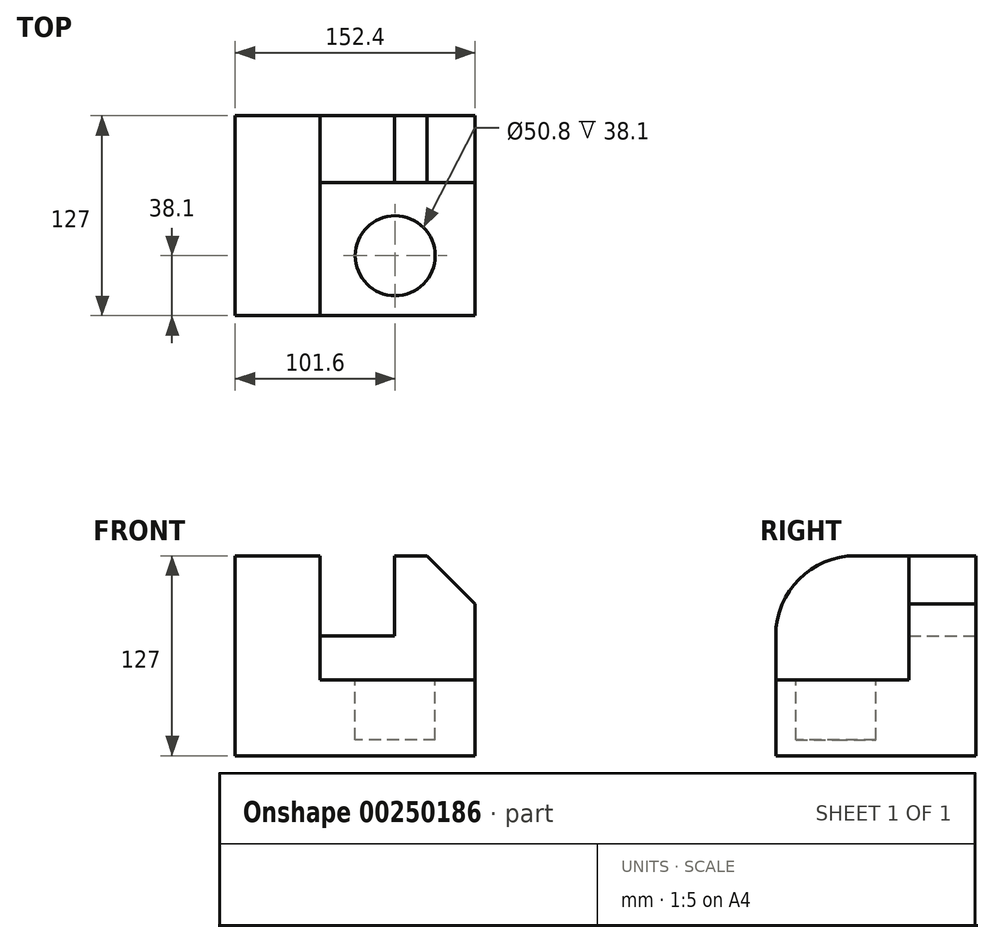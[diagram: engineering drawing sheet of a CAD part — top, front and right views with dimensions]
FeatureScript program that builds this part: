
annotation { "Feature Type Name" : "Feature", "Feature Type Description" : "" }
export const myFeature = defineFeature(function(context is Context, id is Id, definition is map)
    precondition{}
    {
        {
            var Q0;
            Q0=qCreatedBy(makeId("Top.planeOp"),FACE);
            var sketch = newSketch(context, id + "F0", { "sketchPlane" : qUnion([Q0])});
            skLineSegment(sketch, "E0.bottom", {"start": v(76.2, 63.5) * mm, "end": v(-76.2, 63.5) * mm});
            skLineSegment(sketch, "E0.top", {"start": v(76.2, -63.5) * mm, "end": v(-76.2, -63.5) * mm});
            skLineSegment(sketch, "E0.left", {"start": v(76.2, 63.5) * mm, "end": v(76.2, -63.5) * mm});
            skLineSegment(sketch, "E0.right", {"start": v(-76.2, 63.5) * mm, "end": v(-76.2, -63.5) * mm});
            skPoint(sketch, "E0.middle", {"position": v(0, 0) * mm});
            skSolve(sketch);
        }
        {
            var Q0;
            Q0=makeQuery(id+"F0.imprint","IMPRINT",FACE,{"disambiguationData":[TD([[makeQuery(id+"F0.imprint","IMPRINT",EDGE,{"derivedFrom":sQuery(id+"F0.wireOp",EDGE,"E0.bottom")}),1.0]])]});
            extrude(context, id + "F1", {"entities" : qUnion([Q0]), "depth" : 127 * mm});
        }
        {
            var Q0;
            Q0=makeQuery(id+"F1.opExtrude","CAP_FACE",FACE,{"disambiguationData":[OSD([sQuery(id+"F0.wireOp",EDGE,"E0.bottom"),sQuery(id+"F0.wireOp",EDGE,"E0.top"),sQuery(id+"F0.wireOp",EDGE,"E0.left"),sQuery(id+"F0.wireOp",EDGE,"E0.right")])],"isStart":false});
            var sketch = newSketch(context, id + "F2", { "sketchPlane" : qUnion([Q0])});
            skLineSegment(sketch, "E1.bottom", {"start": v(-76.2, -63.5) * mm, "end": v(-22.42, -63.5) * mm});
            skLineSegment(sketch, "E1.top", {"start": v(-76.2, -24.2) * mm, "end": v(-22.42, -24.2) * mm});
            skLineSegment(sketch, "E1.left", {"start": v(-76.2, -63.5) * mm, "end": v(-76.2, -24.2) * mm});
            skLineSegment(sketch, "E1.right", {"start": v(-22.42, -63.5) * mm, "end": v(-22.42, -24.2) * mm});
            skLineSegment(sketch, "E2.bottom", {"start": v(-22.42, -24.2) * mm, "end": v(-76.2, -24.2) * mm});
            skLineSegment(sketch, "E2.top", {"start": v(-22.42, 63.5) * mm, "end": v(-76.2, 63.5) * mm});
            skLineSegment(sketch, "E2.left", {"start": v(-22.42, -24.2) * mm, "end": v(-22.42, 63.5) * mm});
            skLineSegment(sketch, "E2.right", {"start": v(-76.2, -24.2) * mm, "end": v(-76.2, 63.5) * mm});
            skLineSegment(sketch, "E3.bottom", {"start": v(-22.42, 63.5) * mm, "end": v(25.1, 63.5) * mm});
            skLineSegment(sketch, "E3.top", {"start": v(-22.42, 21.07) * mm, "end": v(25.1, 21.07) * mm});
            skLineSegment(sketch, "E3.left", {"start": v(-22.42, 63.5) * mm, "end": v(-22.42, 21.07) * mm});
            skLineSegment(sketch, "E3.right", {"start": v(25.1, 63.5) * mm, "end": v(25.1, 21.07) * mm});
            skLineSegment(sketch, "E4.top", {"start": v(25.1, 21.07) * mm, "end": v(40.8, 21.07) * mm});
            skLineSegment(sketch, "E5.bottom", {"start": v(-22.42, 21.07) * mm, "end": v(76.2, 21.07) * mm});
            skLineSegment(sketch, "E5.top", {"start": v(-22.42, -63.5) * mm, "end": v(76.2, -63.5) * mm});
            skLineSegment(sketch, "E5.left", {"start": v(-22.42, 21.07) * mm, "end": v(-22.42, -63.5) * mm});
            skLineSegment(sketch, "E5.right", {"start": v(76.2, 21.07) * mm, "end": v(76.2, -63.5) * mm});
            skLineSegment(sketch, "E6", {"start": v(76.2, 63.5) * mm, "end": v(76.2, 21.07) * mm});
            skLineSegment(sketch, "E7", {"start": v(25.1, 63.5) * mm, "end": v(76.2, 63.5) * mm});
            skLineSegment(sketch, "E8", {"start": v(40.8, 21.07) * mm, "end": v(40.8, 63.5) * mm});
            skSolve(sketch);
        }
        {
            var Q0;
            {var subQ0=sQuery(id+"F2.wireOp",EDGE,"E5.top");Q0=makeQuery(id+"F2.imprint","IMPRINT",FACE,{"disambiguationData":[TD([[makeQuery(id+"F2.imprint","IMPRINT",EDGE,{"derivedFrom":subQ0}),-1.0]])]});}
            extrude(context, id + "F3", {"entities" : qUnion([Q0]), "operationType" : NewBodyOperationType.REMOVE, "oppositeDirection" : true, "depth" : 78.74 * mm});
        }
        {
            var Q0;
            Q0=makeQuery(id+"F2.imprint","IMPRINT",FACE,{"disambiguationData":[TD([[makeQuery(id+"F2.imprint","IMPRINT",EDGE,{"derivedFrom":sQuery(id+"F2.wireOp",EDGE,"E3.bottom")}),1.0]])]});
            extrude(context, id + "F4", {"entities" : qUnion([Q0]), "operationType" : NewBodyOperationType.REMOVE, "oppositeDirection" : true, "depth" : 50.8 * mm});
        }
        {
            var Q0;
            Q0=makeQuery(id+"F1.opExtrude","CAP_EDGE",EDGE,{"disambiguationData":[OSD([sQuery(id+"F0.wireOp",EDGE,"E0.left")])],"isStart":false});
            chamfer(context, id + "F5", {"entities" : qUnion([Q0]), "width" : 30.48 * mm, "tangentPropagation" : true});
        }
        {
            var Q0;
            Q0=makeQuery(id+"F3.boolean.opBoolean","COPY",FACE,{"derivedFrom":makeQuery(id+"F3.opExtrude","CAP_FACE",FACE,{"disambiguationData":[OSD([sQuery(id+"F2.wireOp",EDGE,"E5.bottom"),sQuery(id+"F2.wireOp",EDGE,"E5.top"),sQuery(id+"F2.wireOp",EDGE,"E5.left"),sQuery(id+"F2.wireOp",EDGE,"E5.right")])],"isStart":false})});
            var sketch = newSketch(context, id + "F6", { "sketchPlane" : qUnion([Q0])});
            skCircle(sketch, "E9", {"center": v(25.4, -25.4) * mm, "radius": 25.4 * mm});
            skSolve(sketch);
        }
        {
            var Q0;
            Q0 = qSketchRegion(id + "F6", true);
            extrude(context, id + "F7", {"entities" : qUnion([Q0]), "operationType" : NewBodyOperationType.REMOVE, "oppositeDirection" : true, "depth" : 38.1 * mm});
        }
        {
            var Q0;
            Q0=makeQuery(id+"F1.opExtrude","CAP_EDGE",EDGE,{"disambiguationData":[OSD([sQuery(id+"F0.wireOp",EDGE,"E0.top")])],"isStart":false});
            fillet(context, id + "F8", {"entities" : qUnion([Q0]), "radius" : 50.8 * mm, "tangentPropagation" : true, "allowEdgeOverflow" : false});
        }
    });
